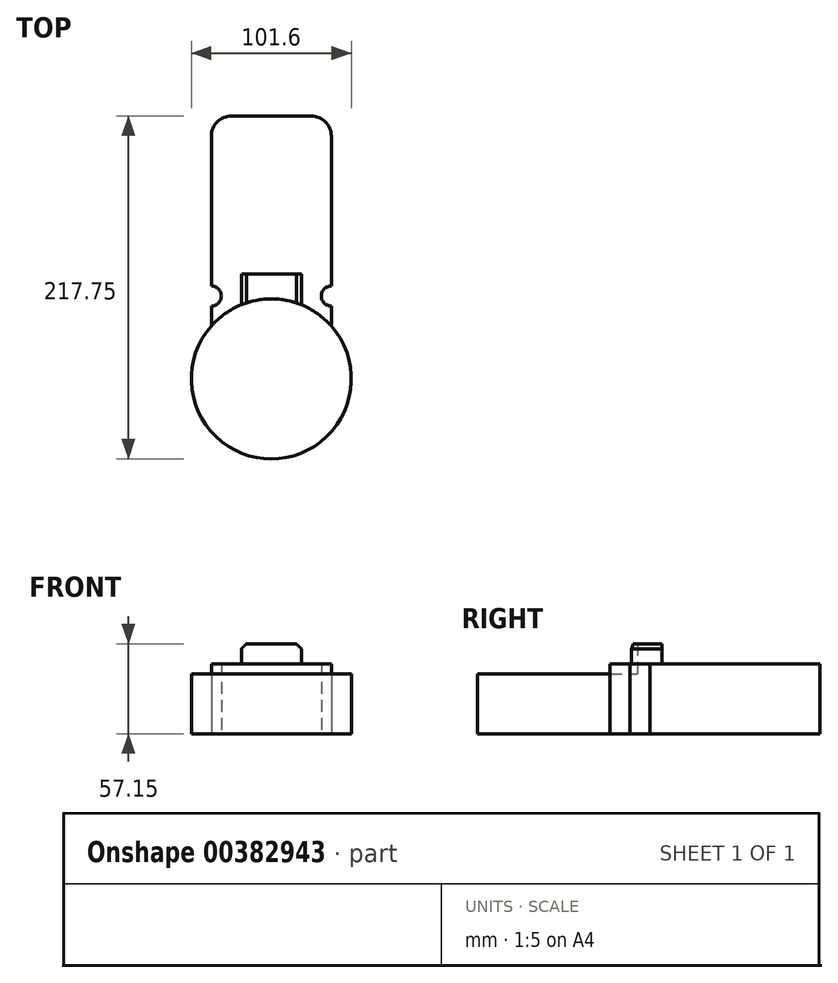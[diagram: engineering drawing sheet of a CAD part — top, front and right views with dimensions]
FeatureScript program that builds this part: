
annotation { "Feature Type Name" : "Feature", "Feature Type Description" : "" }
export const myFeature = defineFeature(function(context is Context, id is Id, definition is map)
    precondition{}
    {
        {
            var Q0;
            Q0=qCreatedBy(makeId("Top.planeOp"),FACE);
            var sketch = newSketch(context, id + "F0", { "sketchPlane" : qUnion([Q0])});
            skLineSegment(sketch, "E0.bottom", {"start": v(-38.1, 66.68) * mm, "end": v(38.1, 66.68) * mm});
            skLineSegment(sketch, "E0.top", {"start": v(-38.1, -66.68) * mm, "end": v(38.1, -66.68) * mm});
            skLineSegment(sketch, "E0.left", {"start": v(-38.1, 66.68) * mm, "end": v(-38.1, -66.68) * mm});
            skLineSegment(sketch, "E0.right", {"start": v(38.1, 66.68) * mm, "end": v(38.1, -66.68) * mm});
            skPoint(sketch, "E0.middle", {"position": v(0, 0) * mm});
            skCircle(sketch, "E1", {"center": v(0, 100.28) * mm, "radius": 50.8 * mm});
            skPoint(sketch, "E1.third.point", {"position": v(45.2, 123.46) * mm});
            skCircle(sketch, "E2", {"center": v(-38.1, 47.62) * mm, "radius": 6.35 * mm});
            skCircle(sketch, "E3.MirrorC", {"center": v(38.1, 47.62) * mm, "radius": 6.35 * mm});
            skSolve(sketch);
        }
        {
            var Q0;
            {var subQ7=sQuery(id+"F0.wireOp",EDGE,"E0.top");Q0=makeQuery(id+"F0.imprint","IMPRINT",FACE,{"disambiguationData":[TD([[makeQuery(id+"F0.imprint","IMPRINT",EDGE,{"derivedFrom":subQ7}),1.0]])]});}
            var Q1;
            {var subQ0=sQuery(id+"F0.wireOp",EDGE,"E2");var subQ1=sQuery(id+"F0.wireOp",EDGE,"E0.left");var subQ2=makeQuery(id+"F0.imprint","INTERSECT",VERTEX,{"disambiguationData":[OD(0.0)],"derivedFrom":[subQ1,subQ0]});Q1=makeQuery(id+"F0.imprint","IMPRINT",FACE,{"disambiguationData":[TD([[makeQuery(id+"F0.imprint","IMPRINT",EDGE,{"disambiguationData":[TD([[subQ2,-1.0]])],"derivedFrom":subQ1}),-1.0]])]});}
            var Q2;
            {var subQ0=sQuery(id+"F0.wireOp",EDGE,"E3.MirrorC");var subQ1=sQuery(id+"F0.wireOp",EDGE,"E0.right");var subQ2=makeQuery(id+"F0.imprint","INTERSECT",VERTEX,{"disambiguationData":[OD(0.0)],"derivedFrom":[subQ1,subQ0]});Q2=makeQuery(id+"F0.imprint","IMPRINT",FACE,{"disambiguationData":[TD([[makeQuery(id+"F0.imprint","IMPRINT",EDGE,{"disambiguationData":[TD([[subQ2,-1.0]])],"derivedFrom":subQ1}),1.0]])]});}
            var Q3;
            {var subQ0=sQuery(id+"F0.wireOp",EDGE,"E2");var subQ1=sQuery(id+"F0.wireOp",EDGE,"E0.left");var subQ2=makeQuery(id+"F0.imprint","INTERSECT",VERTEX,{"disambiguationData":[OD(0.0)],"derivedFrom":[subQ1,subQ0]});Q3=makeQuery(id+"F0.imprint","IMPRINT",FACE,{"disambiguationData":[TD([[makeQuery(id+"F0.imprint","IMPRINT",EDGE,{"disambiguationData":[TD([[subQ2,-1.0]])],"derivedFrom":subQ1}),1.0]])]});}
            var Q4;
            {var subQ0=sQuery(id+"F0.wireOp",EDGE,"E3.MirrorC");var subQ1=sQuery(id+"F0.wireOp",EDGE,"E0.right");var subQ2=makeQuery(id+"F0.imprint","INTERSECT",VERTEX,{"disambiguationData":[OD(0.0)],"derivedFrom":[subQ1,subQ0]});Q4=makeQuery(id+"F0.imprint","IMPRINT",FACE,{"disambiguationData":[TD([[makeQuery(id+"F0.imprint","IMPRINT",EDGE,{"disambiguationData":[TD([[subQ2,-1.0]])],"derivedFrom":subQ1}),-1.0]])]});}
            extrude(context, id + "F1", {"entities" : qUnion([Q0, Q1, Q2, Q3, Q4]), "depth" : 44.45 * mm});
        }
        {
            var Q0;
            {var subQ0=sQuery(id+"F0.wireOp",EDGE,"E0.bottom");Q0=makeQuery(id+"F0.imprint","IMPRINT",FACE,{"disambiguationData":[TD([[makeQuery(id+"F0.imprint","IMPRINT",EDGE,{"derivedFrom":subQ0}),1.0]])]});}
            var Q1;
            {var subQ0=sQuery(id+"F0.wireOp",EDGE,"E0.bottom");Q1=makeQuery(id+"F0.imprint","IMPRINT",FACE,{"disambiguationData":[TD([[makeQuery(id+"F0.imprint","IMPRINT",EDGE,{"derivedFrom":subQ0}),-1.0]])]});}
            extrude(context, id + "F2", {"entities" : qUnion([Q0, Q1]), "operationType" : NewBodyOperationType.ADD, "depth" : 38.1 * mm});
        }
        {
            var Q0;
            Q0=qCreatedBy(makeId("Right.planeOp"),FACE);
            var sketch = newSketch(context, id + "F3", { "sketchPlane" : qUnion([Q0])});
            skLineSegment(sketch, "E4", {"start": v(0, 36.55) * mm, "end": v(0, 13.81) * mm});
            skSolve(sketch);
        }
        {
            var Q0;
            Q0=makeQuery(id+"F1.opExtrude","SWEPT_EDGE",EDGE,{"disambiguationData":[OSD([sQuery(id+"F0.wireOp",EDGE,"E0.top"),sQuery(id+"F0.wireOp",EDGE,"E0.left")])]});
            var Q1;
            Q1=makeQuery(id+"F1.opExtrude","SWEPT_EDGE",EDGE,{"disambiguationData":[OSD([sQuery(id+"F0.wireOp",EDGE,"E0.top"),sQuery(id+"F0.wireOp",EDGE,"E0.right")])]});
            fillet(context, id + "F4", {"entities" : qUnion([Q0, Q1]), "radius" : 12.7 * mm, "tangentPropagation" : true, "allowEdgeOverflow" : false});
        }
        {
            var Q0;
            Q0=makeQuery(id+"F1.opExtrude","SWEPT_BODY",BODY,{"disambiguationData":[OSD([sQuery(id+"F0.wireOp",EDGE,"E0.top"),sQuery(id+"F0.wireOp",EDGE,"E0.left"),sQuery(id+"F0.wireOp",EDGE,"E0.right"),sQuery(id+"F0.wireOp",EDGE,"E1"),sQuery(id+"F0.wireOp",EDGE,"E2"),sQuery(id+"F0.wireOp",EDGE,"E3.MirrorC")])]});
            var Q1;
            Q1=sQuery(id+"F3.wireOp",EDGE,"E4");
            transform(context, id + "F5", {"entities" : qUnion([Q0]), "transformType" : TransformType.ROTATION, "transformAxis" : qUnion([Q1]), "angle" : 180 * degree, "makeCopy" : false});
        }
        {
            var Q0;
            Q0=makeQuery(id+"F1.opExtrude","CAP_FACE",FACE,{"disambiguationData":[OSD([sQuery(id+"F0.wireOp",EDGE,"E0.top"),sQuery(id+"F0.wireOp",EDGE,"E0.left"),sQuery(id+"F0.wireOp",EDGE,"E0.right"),sQuery(id+"F0.wireOp",EDGE,"E1"),sQuery(id+"F0.wireOp",EDGE,"E2"),sQuery(id+"F0.wireOp",EDGE,"E3.MirrorC")])],"isStart":false});
            var sketch = newSketch(context, id + "F6", { "sketchPlane" : qUnion([Q0])});
            skLineSegment(sketch, "E5.bottom", {"start": v(19.05, 47.63) * mm, "end": v(-19.05, 47.63) * mm});
            skLineSegment(sketch, "E5.top", {"start": v(19.05, -53.97) * mm, "end": v(-19.05, -53.97) * mm});
            skLineSegment(sketch, "E5.left", {"start": v(19.05, 47.63) * mm, "end": v(19.05, -53.98) * mm});
            skLineSegment(sketch, "E5.right", {"start": v(-19.05, 47.63) * mm, "end": v(-19.05, -53.97) * mm});
            skPoint(sketch, "E5.middle", {"position": v(0, -3.17) * mm});
            skArc(sketch, "E6", {"start": v(19.05, -53.18) * mm, "mid": v(0, -49.46) * mm, "end": v(-19.05, -53.18) * mm});
            skLineSegment(sketch, "E7", {"start": v(-19.05, -33.66) * mm, "end": v(19.05, -33.66) * mm});
            skSolve(sketch);
        }
        {
            var Q0;
            {var subQ0=sQuery(id+"F6.wireOp",EDGE,"E6");Q0=makeQuery(id+"F6.imprint","IMPRINT",FACE,{"disambiguationData":[TD([[makeQuery(id+"F6.imprint","IMPRINT",EDGE,{"derivedFrom":subQ0}),-1.0]])]});}
            extrude(context, id + "F7", {"entities" : qUnion([Q0]), "operationType" : NewBodyOperationType.ADD, "depth" : 12.7 * mm});
        }
        {
            var Q0;
            Q0=makeQuery(id+"F7.opExtrude","CAP_EDGE",EDGE,{"disambiguationData":[OSD([sQuery(id+"F6.wireOp",EDGE,"E5.right")])],"isStart":false});
            var Q1;
            Q1=makeQuery(id+"F7.opExtrude","CAP_EDGE",EDGE,{"disambiguationData":[OSD([sQuery(id+"F6.wireOp",EDGE,"E5.left")])],"isStart":false});
            chamfer(context, id + "F8", {"entities" : qUnion([Q0, Q1]), "width" : 3.17 * mm});
        }
    });
